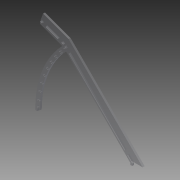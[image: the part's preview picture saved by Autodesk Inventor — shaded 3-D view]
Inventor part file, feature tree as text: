
AUTODESK INVENTOR PART (.ipt)
format: ipt  version: 2013 (Build 170138000, 138)  size: 218,624 bytes
history: native  units: in
note: dims shown in document units (in); Inventor stores cm internally (conversion verified against a paired STEP export)
features: reference x11, extrude x7, sketch x7
ambient origin geometry x8: Origin, YZ Plane, XZ Plane, XY Plane, X Axis, Y Axis, Z Axis, Center Point
bodies: Solid1 (feature_tree)
feature tree (25):
  extrude  "Extrusion1"  Depth=0.25in TaperAngle=0.0deg
  extrude  "Extrusion2"  Depth=0.25in
  extrude  "Extrusion3"  Depth=0.25in TaperAngle=0.0deg
  extrude  "Extrusion4"  Depth=1.0in
  extrude  "Extrusion7"  Depth=0.25in TaperAngle=0.0deg
  extrude  "Extrusion8"  Depth=1.375in
  extrude  "Extrusion11"  [1 undecoded]
  sketch  "Sketch1"  dims[d0=23.375in d1=0.25in d2=0.0in]
  sketch  "Sketch2"  dims[d3=0.25in d4=0.25in]
  sketch  "Sketch3"  dims[d5=0.25in d6=0.0in d10=0.25in d11=0.0in]
  reference  "Reference1"
  sketch  "Sketch4"  dims[d12=0.25in d13=0.0in d19=1.0in]
  reference  "Reference2"
  sketch  "Sketch7"  dims[d20=0.7043in d21=0.25in d22=0.0in]
  reference  "Reference5"
  reference  "Reference6"
  reference  "Reference7"
  reference  "Reference8"
  sketch  "Sketch8"  dims[d23=0.25in d24=0.0in d35=1.375in]
  reference  "Reference9"
  reference  "Reference10"
  reference  "Reference11"
  reference  "Reference12"
  reference  "Reference13"
  sketch  "Sketch11"  dims[d36=0.25in d37=0.0in]
note: 1 required parameter value undecoded (feature->parameter linkage not recoverable at this tier; creation-order binding heuristic only, values carry confidence <= 0.55)
